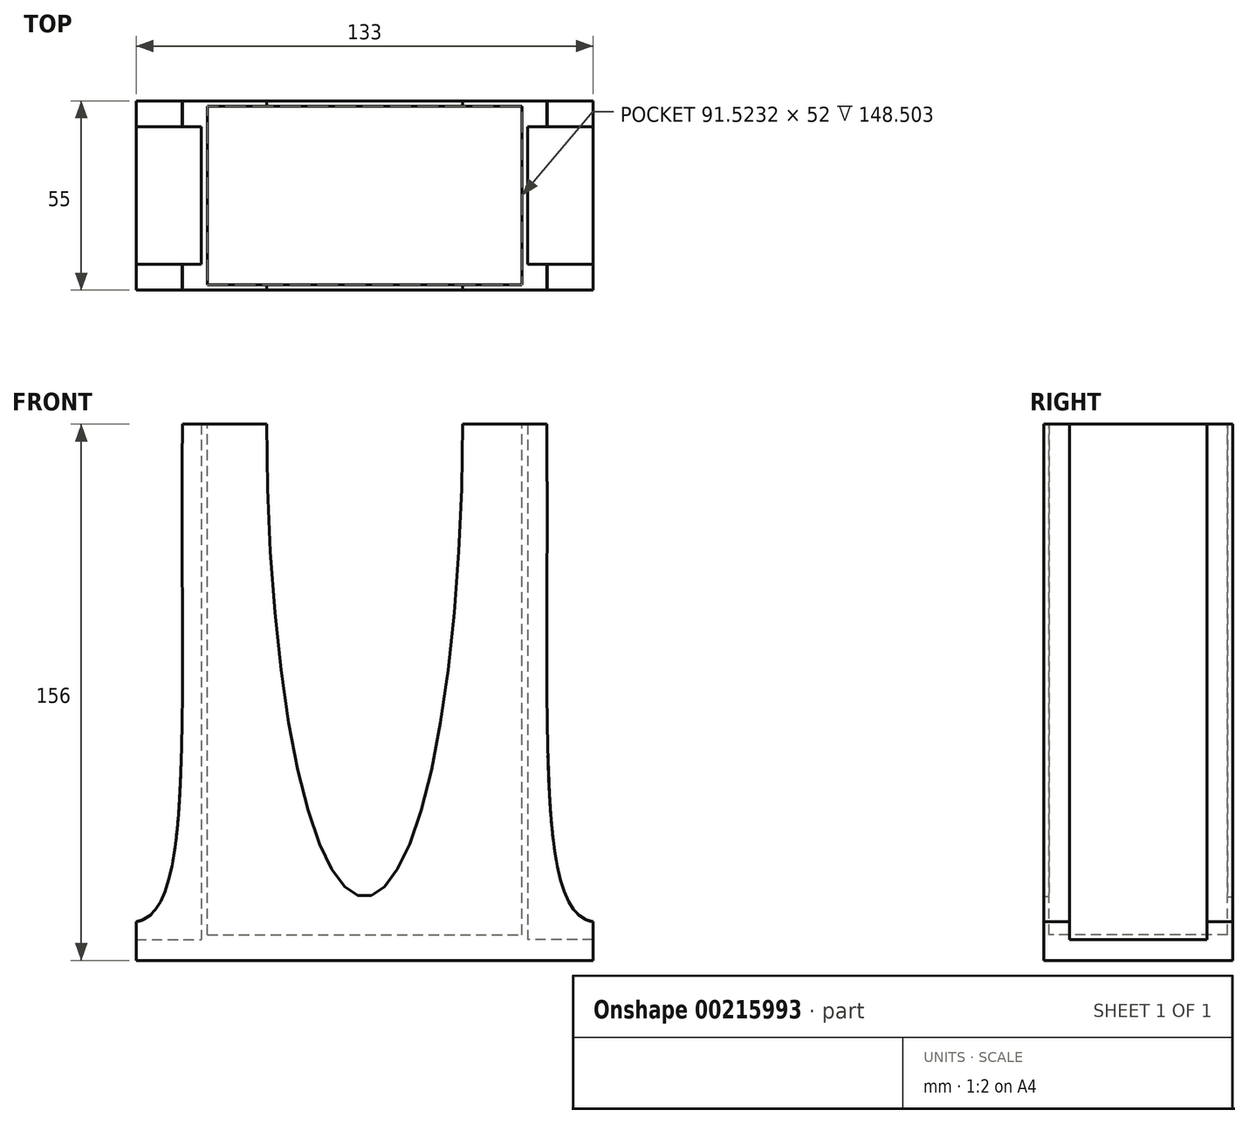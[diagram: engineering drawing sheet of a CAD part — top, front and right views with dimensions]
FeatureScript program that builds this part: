
annotation { "Feature Type Name" : "Feature", "Feature Type Description" : "" }
export const myFeature = defineFeature(function(context is Context, id is Id, definition is map)
    precondition{}
    {
        {
            var Q0;
            Q0=qCreatedBy(makeId("Front.planeOp"),FACE);
            var sketch = newSketch(context, id + "F0", { "sketchPlane" : qUnion([Q0])});
            skLineSegment(sketch, "E0.bottom", {"start": v(47.5, -75) * mm, "end": v(-47.5, -75) * mm});
            skLineSegment(sketch, "E0.top", {"start": v(47.5, 75) * mm, "end": v(-47.5, 75) * mm});
            skLineSegment(sketch, "E0.left", {"start": v(47.5, -75) * mm, "end": v(47.5, 75) * mm});
            skLineSegment(sketch, "E0.right", {"start": v(-47.5, -75) * mm, "end": v(-47.5, 75) * mm});
            skPoint(sketch, "E0.middle", {"position": v(0, 0) * mm});
            skEllipse(sketch, "E1", {"center": v(0, 75) * mm, "majorRadius": 137.5 * mm, "minorRadius": 28.5 * mm, "majorAxis": v(0, -1)});
            skSolve(sketch);
        }
        {
            var Q0;
            Q0=makeQuery(id+"F0.imprint","IMPRINT",FACE,{"disambiguationData":[TD([[makeQuery(id+"F0.imprint","IMPRINT",EDGE,{"derivedFrom":sQuery(id+"F0.wireOp",EDGE,"E0.bottom")}),-1.0]])]});
            var Q1;
            Q1 = qSketchRegion(id + "FPEPpxyTK2O7V2k_1", true);
            var Q2;
            Q2 = qSketchRegion(id + "FPEPpxyTK2O7V2k_1", true);
            extrude(context, id + "F1", {"entities" : qUnion([Q0, Q1, Q2]), "endBound" : BoundingType.SYMMETRIC, "depth" : 55 * mm});
        }
        {
            var Q0;
            Q0=qCreatedBy(makeId("Front.planeOp"),FACE);
            var sketch = newSketch(context, id + "F2", { "sketchPlane" : qUnion([Q0])});
            skLineSegment(sketch, "E2.bottom", {"start": v(-45.76, -73.5) * mm, "end": v(46.24, -73.5) * mm});
            skLineSegment(sketch, "E2.top", {"start": v(-45.76, 86.5) * mm, "end": v(46.24, 86.5) * mm});
            skLineSegment(sketch, "E2.left", {"start": v(-45.76, -73.5) * mm, "end": v(-45.76, 86.5) * mm});
            skLineSegment(sketch, "E2.right", {"start": v(46.24, -73.5) * mm, "end": v(46.24, 86.5) * mm});
            skSolve(sketch);
        }
        {
            var Q0;
            Q0 = qSketchRegion(id + "F2", true);
            extrude(context, id + "F3", {"entities" : qUnion([Q0]), "operationType" : NewBodyOperationType.REMOVE, "endBound" : BoundingType.SYMMETRIC, "oppositeDirection" : true, "depth" : 52 * mm});
        }
        {
            var Q0;
            Q0=qCreatedBy(makeId("Front.planeOp"),FACE);
            var sketch = newSketch(context, id + "F4", { "sketchPlane" : qUnion([Q0])});
            skLineSegment(sketch, "E3.bottom", {"start": v(66.5, 75) * mm, "end": v(47.5, 75) * mm});
            skLineSegment(sketch, "E3.top", {"start": v(66.5, -75) * mm, "end": v(47.5, -75) * mm});
            skLineSegment(sketch, "E3.left", {"start": v(66.5, 75) * mm, "end": v(66.5, -75) * mm});
            skLineSegment(sketch, "E3.right", {"start": v(47.5, 75) * mm, "end": v(47.5, -75) * mm});
            skPoint(sketch, "E3.middle", {"position": v(57, 0) * mm});
            skFitSpline(sketch, "E4", {"points": [v(53, 75) * mm, v(66.5, -69.74) * mm], "startDerivative": vector(2.35, -262.52) * mm, "endDerivative": vector(51.36, -6.87) * mm});
            skSolve(sketch);
        }
        {
            var Q0;
            {var subQ1=sQuery(id+"F4.wireOp",EDGE,"E3.top");Q0=makeQuery(id+"F4.imprint","IMPRINT",FACE,{"disambiguationData":[TD([[makeQuery(id+"F4.imprint","IMPRINT",EDGE,{"derivedFrom":subQ1}),-1.0]])]});}
            var Q1;
            Q1 = qSketchRegion(id + "FRbqfso3bPIoW3i_1", true);
            var Q2;
            Q2=makeQuery(id+"F1.opExtrude","CAP_FACE",FACE,{"disambiguationData":[OSD([sQuery(id+"F0.wireOp",EDGE,"E0.bottom"),sQuery(id+"F0.wireOp",EDGE,"E0.top"),sQuery(id+"F0.wireOp",EDGE,"E0.left"),sQuery(id+"F0.wireOp",EDGE,"E0.right"),sQuery(id+"F0.wireOp",EDGE,"E1")])],"isStart":false});
            extrude(context, id + "F5", {"entities" : qUnion([Q0, Q1]), "operationType" : NewBodyOperationType.ADD, "endBound" : BoundingType.UP_TO_SURFACE, "endBoundEntityFace" : qUnion([Q2]), "depth" : 12 * mm, "hasSecondDirection" : true, "secondDirectionOppositeDirection" : false, "secondDirectionDepth" : 20 * mm});
        }
        {
            var Q0;
            Q0=makeQuery(id+"F1.opExtrude","SWEPT_BODY",BODY,{"disambiguationData":[OSD([sQuery(id+"F0.wireOp",EDGE,"E0.bottom"),sQuery(id+"F0.wireOp",EDGE,"E0.top"),sQuery(id+"F0.wireOp",EDGE,"E0.left"),sQuery(id+"F0.wireOp",EDGE,"E0.right"),sQuery(id+"F0.wireOp",EDGE,"E1")])]});
            var Q1;
            Q1=qCreatedBy(makeId("Right.planeOp"),FACE);
            mirror(context, id + "F6", {"operationType" : NewBodyOperationType.ADD, "entities" : qUnion([Q0]), "mirrorPlane" : qUnion([Q1])});
        }
        {
            var Q0;
            Q0=makeQuery(id+"F1.opExtrude","SWEPT_BODY",BODY,{"disambiguationData":[OSD([sQuery(id+"F0.wireOp",EDGE,"E0.bottom"),sQuery(id+"F0.wireOp",EDGE,"E0.top"),sQuery(id+"F0.wireOp",EDGE,"E0.left"),sQuery(id+"F0.wireOp",EDGE,"E0.right"),sQuery(id+"F0.wireOp",EDGE,"E1")])]});
            var Q1;
            Q1=qCreatedBy(makeId("Front.planeOp"),FACE);
            mirror(context, id + "F7", {"operationType" : NewBodyOperationType.ADD, "entities" : qUnion([Q0]), "mirrorPlane" : qUnion([Q1])});
        }
        {
            var Q0;
            Q0=qCreatedBy(makeId("Front.planeOp"),FACE);
            var sketch = newSketch(context, id + "F8", { "sketchPlane" : qUnion([Q0])});
            skLineSegment(sketch, "E5.bottom", {"start": v(-66.5, -75) * mm, "end": v(66.5, -75) * mm});
            skLineSegment(sketch, "E5.top", {"start": v(-66.5, -81) * mm, "end": v(66.5, -81) * mm});
            skLineSegment(sketch, "E5.left", {"start": v(-66.5, -75) * mm, "end": v(-66.5, -81) * mm});
            skLineSegment(sketch, "E5.right", {"start": v(66.5, -75) * mm, "end": v(66.5, -81) * mm});
            skSolve(sketch);
        }
        {
            var Q0;
            Q0 = qSketchRegion(id + "F8", true);
            extrude(context, id + "F9", {"entities" : qUnion([Q0]), "operationType" : NewBodyOperationType.ADD, "endBound" : BoundingType.SYMMETRIC, "depth" : 55 * mm});
        }
    });
